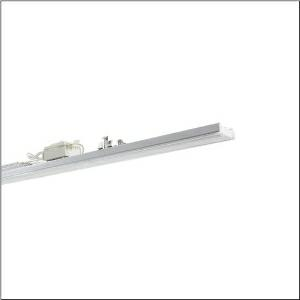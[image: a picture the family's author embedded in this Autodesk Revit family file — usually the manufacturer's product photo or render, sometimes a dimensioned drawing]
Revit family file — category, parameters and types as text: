
# Revit family: licross_21_recessed_mo_52tl11dn48xg
name_source: partatom
category: Lighting Fixtures
units: mm (PartAtom-declared; Revit-internal decimal feet)

## family parameters
Cut with Voids When Loaded = No
Host = Face
Light Source = No
Part Type = Normal
Room Calculation Point = No
Round Connector Dimension = Use Diameter
Shared = No

## types (1)
- --- (1 x LED, 8000 lm, 45 W, 4000K)
    Apparent Load = 45 VA
    CIE Flux Codes = 89 96 99 100 100
    Color Rendering = 80
    Color Temperature = 4000K
    Default Elevation = 1800 mm
    Description = Licross 21 Recessed MO, luminaire insert, of sheet steel, galvanised, coil coated, white, length: 1.500mm, width: 66mm, height: 67mm, LED rated luminous flux: 8.000lm, light colour: 840, SDCM (Standard Deviation of Colour Matching)MacAdam ≤ 3 SDCM (initial), control gear: DALI 2, with plug, 5-pole, with phase selection, mains connection: 220..240V, AC, 50/60Hz, rated input power: 45W, internal wiring halogen-free, primary light control with lens, of plastic, primary optical cover: cover, of PMMA, light emission: direct distribution, primary light characteristic: symmetric, protection rating (complete): IP40, insulation class (complete): insulation class I (protective earthing), certification: CE, ENEC, VDE, UKCA, protection symbol: D if used in an environment without relevant dust loads with corresponding accessories, impact resistance: IK06, permissible ambient temperature for indoor applications: -25..+35°C, corresponds to IFS (International Featured Standards) requirements for safety and quality in the food industry, reducing of maximum allowable ambient temperature of 5°C with ceiling mounting, LABS conformity tested according to VDMA 24364:2018-05, The light source and the operating device comply with the requirements of the Ecodesign Regulation (EU) 2019/2020 and are replaceable in accordance with this regulation, packaging unit: 1 piece
    Height = 58 mm
    Lamp = 1 x LED
    Lamp Light Flux = 8000 lm
    Lamp Power = 45 W
    Lamp count = 1
    Length = 1500 mm
    Luminous efficacy = 178 lm/W
    Manufacturer = Siteco
    ModVariant = No
    Model = 52TL11DN48XG
    Mounting Place = Ceiling
    Mounting Type = Pendant
    Number of Poles = 1
    OnlyDefault = Yes
    Power Factor = 1
    Product Name = Licross 21 Recessed MO
    Product group = luminaire insert | ceiling pendant
    ProductGroupID = 901
    Protection Class = Protection class I
    Protection Degree = IP 40
    RLX_Detail_Level = 1
    RLX_Emergency_Light_Flux = 0 lm
    RLX_Emergency_Type = 0
    RLX_Emergency_Type_DB = No
    RlxData = <blob elided: 24801 chars, md5=e5dcf0a8>
    Socket = socket
    Standby Power = 0 W
    System Light Flux = 8000 lm
    System Power = 45 W
    Type Comments = factory setting: luminous flux: 100 % | dim-lin: 254 | 302 mA
    Type Image = l_1296930.jpg
    URL = http://relux.com
    VarID = @adj_127015
    Voltage = 0 V
    Weight = 0.00 kg
    Width = 66 mm

## geometry (parser evidence)
native form markers: Blend x4, Sweep x10
no freeform markers — native parametric forms only
